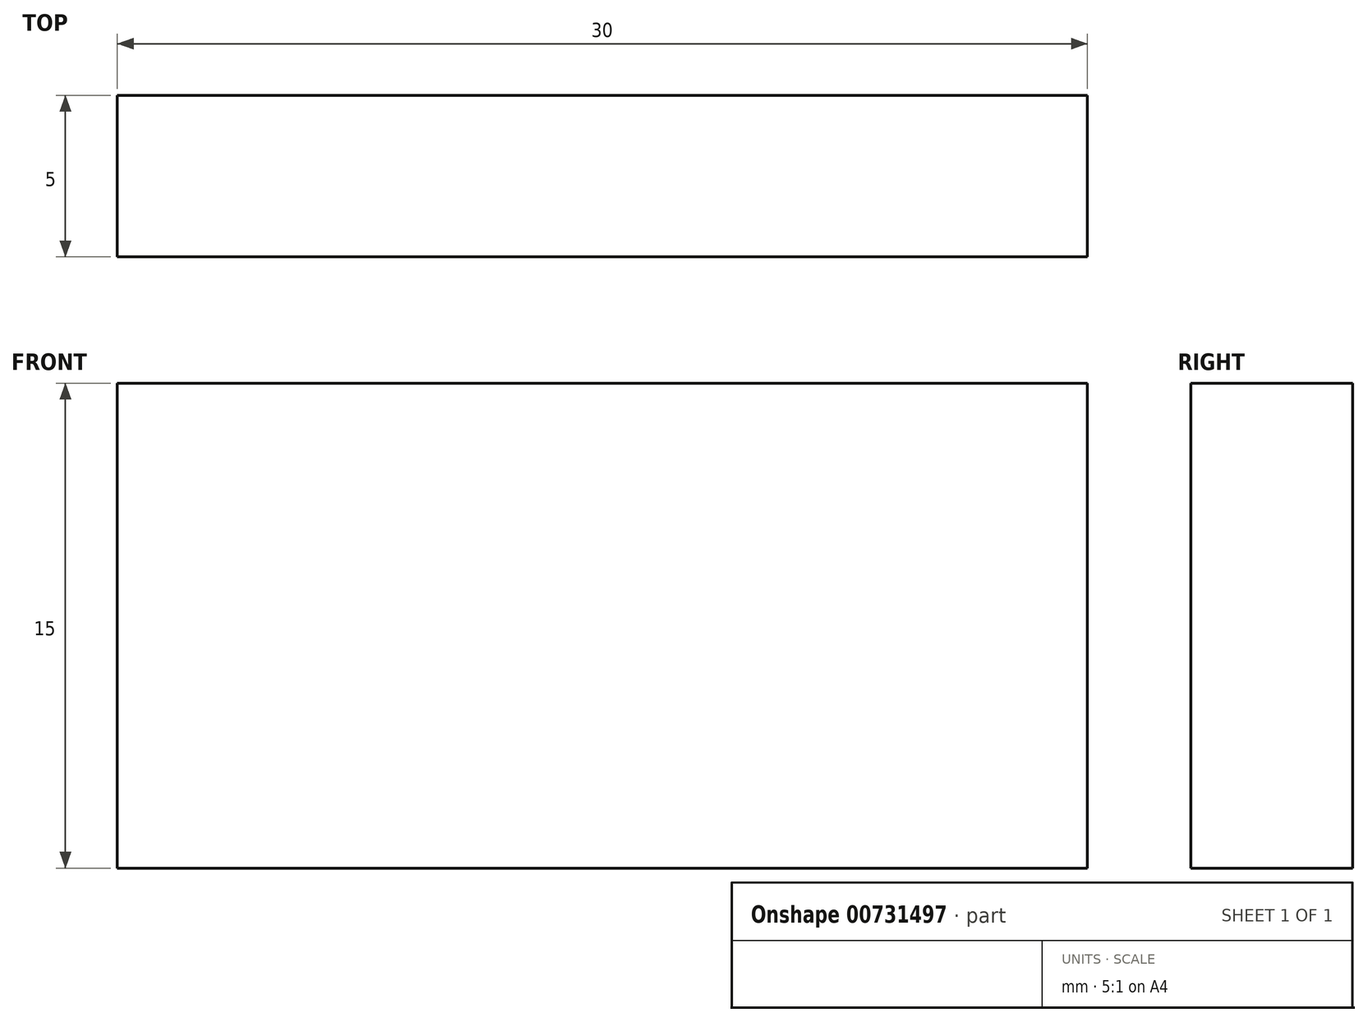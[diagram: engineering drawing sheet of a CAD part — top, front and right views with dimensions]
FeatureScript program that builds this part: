
annotation { "Feature Type Name" : "Feature", "Feature Type Description" : "" }
export const myFeature = defineFeature(function(context is Context, id is Id, definition is map)
    precondition{}
    {
        {
            var Q0;
            Q0=qCreatedBy(makeId("Top.planeOp"),FACE);
            var sketch = newSketch(context, id + "F0", { "sketchPlane" : qUnion([Q0])});
            skLineSegment(sketch, "E0.bottom", {"start": v(15, -2.5) * mm, "end": v(-15, -2.5) * mm});
            skLineSegment(sketch, "E0.top", {"start": v(15, 2.5) * mm, "end": v(-15, 2.5) * mm});
            skLineSegment(sketch, "E0.left", {"start": v(15, -2.5) * mm, "end": v(15, 2.5) * mm});
            skLineSegment(sketch, "E0.right", {"start": v(-15, -2.5) * mm, "end": v(-15, 2.5) * mm});
            skPoint(sketch, "E0.middle", {"position": v(0, 0) * mm});
            skSolve(sketch);
        }
        {
            var Q0;
            Q0 = qSketchRegion(id + "F0", true);
            extrude(context, id + "F1", {"entities" : qUnion([Q0]), "depth" : 15 * mm, "offsetDistance" : 25.4 * mm});
        }
    });
